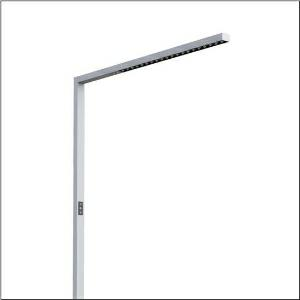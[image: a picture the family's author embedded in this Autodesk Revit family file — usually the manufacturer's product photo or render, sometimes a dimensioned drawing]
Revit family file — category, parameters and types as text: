
# Revit family: silica_r__31_floor_51my52fa3cs_6121
name_source: partatom
category: Lighting Fixtures
units: mm (PartAtom-declared; Revit-internal decimal feet)

## family parameters
Cut with Voids When Loaded = No
Host = Face
Light Source = No
Part Type = Normal
Room Calculation Point = No
Round Connector Dimension = Use Diameter
Shared = No

## types (1)
- Silica® 31 Floor (1 x LED, 10300 lm, 75 W, 3000K)
    Apparent Load = 75 VA
    CIE Flux Codes = 86 100 100 24 100
    Color Rendering = 80
    Color Temperature = 3000K
    Default Elevation = 1800 mm
    Description = Silica® 31 Floor, floorstanding luminaire, secondary optical cover: cover panel, of PMMA, light emission: direct/indirect distribution, primary light characteristic: symmetric, installation type: not mounted, LED, rated luminous flux: 10.300lm, luminous efficacy: 137lm/W, light colour: 830, colour temperature: 3000K, control gear: Touchdim, daylight-dependent control, with cable with plug, mains connection: 230V, AC, 50Hz, connection cable pre-assembled, rated input power: 75W, luminaire head, of aluminium, metallic grey (RAL 9006), length: 1.203mm, width: 52mm, supporting column, angular, of aluminium, metallic grey (RAL 9006), baseplate, of steel, metallic grey (RAL 9006), protection rating (complete): IP20, insulation class (complete): insulation class I (protective earthing), certification: CE, permissible operating ambient temperature: -20..+40°C, standard: EN 50419, packaging unit: 1 piece
    Height = 36 mm
    Lamp = 1 x LED
    Lamp Light Flux = 10300 lm
    Lamp Power = 75 W
    Lamp count = 1
    Length = 1203 mm
    Luminous efficacy = 137 lm/W
    Manufacturer = Siteco
    ModVariant = No
    Model = 51MY52FA3CS
    Mounting Place = Floor
    Mounting Type = Freestanding
    Number of Poles = 1
    OnlyDefault = Yes
    Power Factor = 1
    Product Name = Silica® 31 Floor
    Product group = floorstanding luminaire
    ProductGroupID = 1302
    Protection Class = Protection class I
    Protection Degree = IP 20
    RLX_Detail_Level = 1
    RLX_Emergency_Light_Flux = 0 lm
    RLX_Emergency_Type = 0
    RLX_Emergency_Type_DB = No
    RlxData = <blob elided: 19585 chars, md5=4a4725e6>
    Socket = socket
    Standby Power = 0 W
    System Light Flux = 10300 lm
    System Power = 75 W
    Type Comments = Product without accessories
    Type Image = l_1275303.jpg
    URL = http://relux.com
    VarID = ---
    Voltage = 0 V
    Weight = 0.00 kg
    Width = 52 mm  [stored 0.170604 ft]

note: [stored X ft] marks values corroborated as IEEE doubles in the binary element streams (Revit-internal decimal feet)

## geometry (parser evidence)
native form markers: Blend x4, Sweep x15
no freeform markers — native parametric forms only
